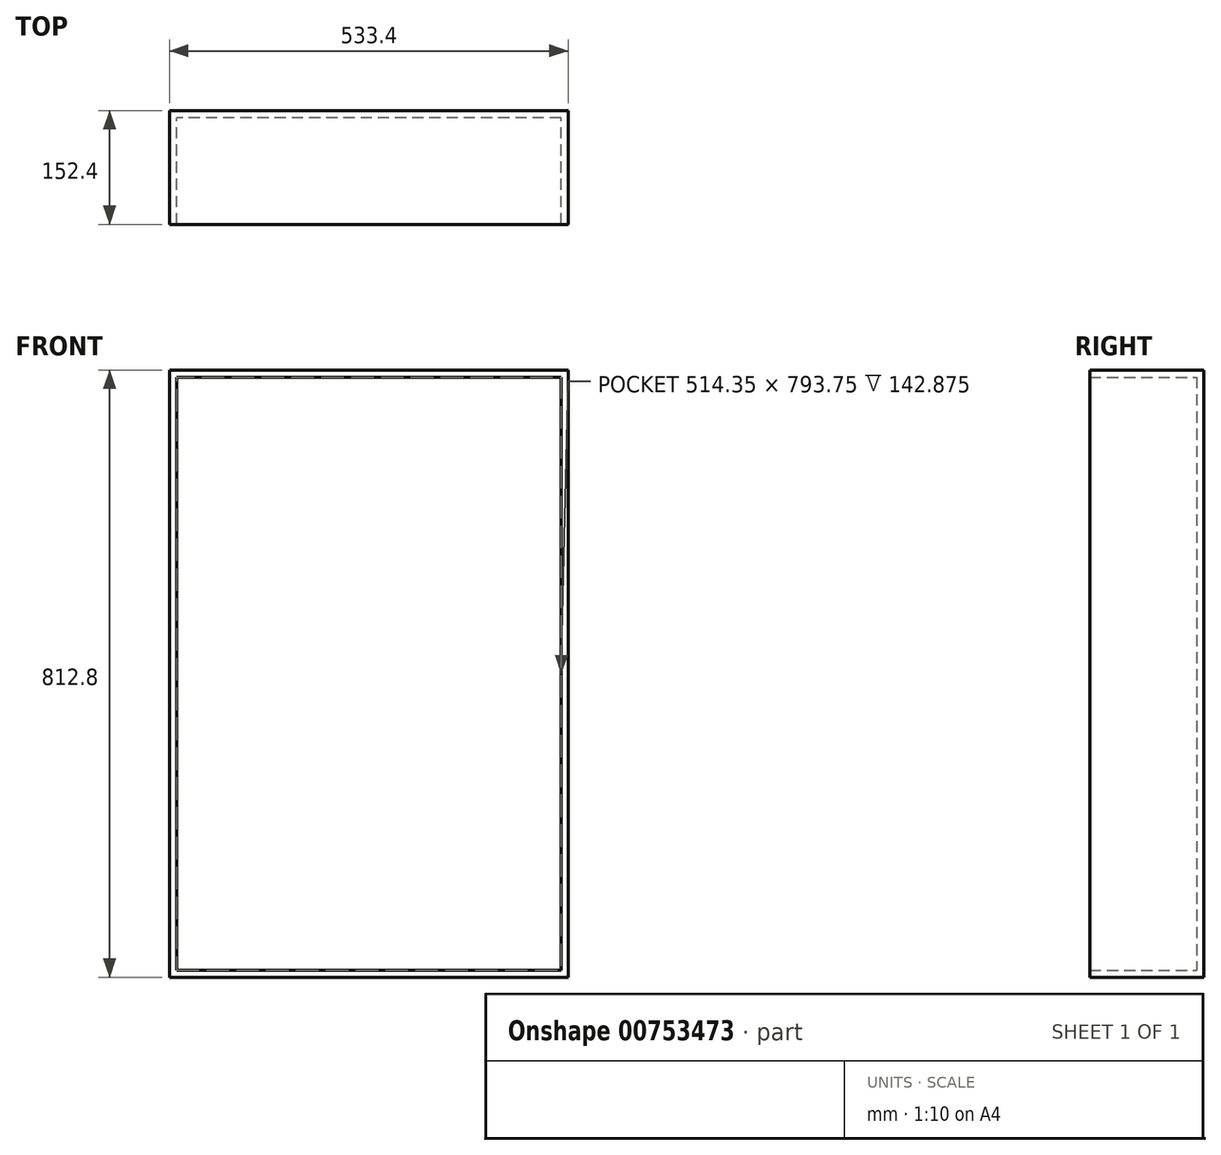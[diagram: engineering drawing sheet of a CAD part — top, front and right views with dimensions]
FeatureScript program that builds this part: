
annotation { "Feature Type Name" : "Feature", "Feature Type Description" : "" }
export const myFeature = defineFeature(function(context is Context, id is Id, definition is map)
    precondition{}
    {
        {
            var Q0;
            Q0=qCreatedBy(makeId("Top.planeOp"),FACE);
            var sketch = newSketch(context, id + "F0", { "sketchPlane" : qUnion([Q0])});
            skLineSegment(sketch, "E0.bottom", {"start": v(0, 0) * mm, "end": v(-609.6, 0) * mm, "construction": true});
            skLineSegment(sketch, "E0.top", {"start": v(0, -254) * mm, "end": v(-609.6, -254) * mm, "construction": true});
            skLineSegment(sketch, "E0.left", {"start": v(0, 0) * mm, "end": v(0, -254) * mm, "construction": true});
            skLineSegment(sketch, "E0.right", {"start": v(-609.6, 0) * mm, "end": v(-609.6, -254) * mm, "construction": true});
            skLineSegment(sketch, "E1.top", {"start": v(0, 609.6) * mm, "end": v(-609.6, 609.6) * mm, "construction": true});
            skLineSegment(sketch, "E1.left", {"start": v(0, 0) * mm, "end": v(0, 609.6) * mm, "construction": true});
            skLineSegment(sketch, "E1.right", {"start": v(-609.6, 0) * mm, "end": v(-609.6, 609.6) * mm, "construction": true});
            skSolve(sketch);
        }
        {
            var Q0;
            Q0=qCreatedBy(makeId("Top.planeOp"),FACE);
            cPlane(context, id + "F1", {"entities" : qUnion([Q0]), "cplaneType" : CPlaneType.OFFSET, "offset" : 50.8 * mm, "width" : 152.4 * mm, "height" : 152.4 * mm});
        }
        {
            var Q0;
            Q0=qCreatedBy(id+"F1.planeOp",FACE);
            var sketch = newSketch(context, id + "F2", { "sketchPlane" : qUnion([Q0])});
            skLineSegment(sketch, "E2.bottom", {"start": v(0, -203.2) * mm, "end": v(-533.4, -203.2) * mm});
            skLineSegment(sketch, "E2.top", {"start": v(0, -50.8) * mm, "end": v(-533.4, -50.8) * mm});
            skLineSegment(sketch, "E2.left", {"start": v(0, -203.2) * mm, "end": v(0, -50.8) * mm});
            skLineSegment(sketch, "E2.right", {"start": v(-533.4, -203.2) * mm, "end": v(-533.4, -50.8) * mm});
            skSolve(sketch);
        }
        {
            var Q0;
            Q0=makeQuery(id+"F2.imprint","IMPRINT",FACE,{"disambiguationData":[TD([[makeQuery(id+"F2.imprint","IMPRINT",EDGE,{"derivedFrom":sQuery(id+"F2.wireOp",EDGE,"E2.bottom")}),-1.0]])]});
            extrude(context, id + "F3", {"entities" : qUnion([Q0]), "depth" : 812.8 * mm, "offsetDistance" : 25.4 * mm});
        }
        {
            var Q0;
            Q0=makeQuery(id+"F3.opExtrude","SWEPT_FACE",FACE,{"disambiguationData":[OSD([sQuery(id+"F2.wireOp",EDGE,"E2.bottom")])]});
            shell(context, id + "F4", {"entities" : qUnion([Q0]), "thickness" : 9.52 * mm});
        }
    });
